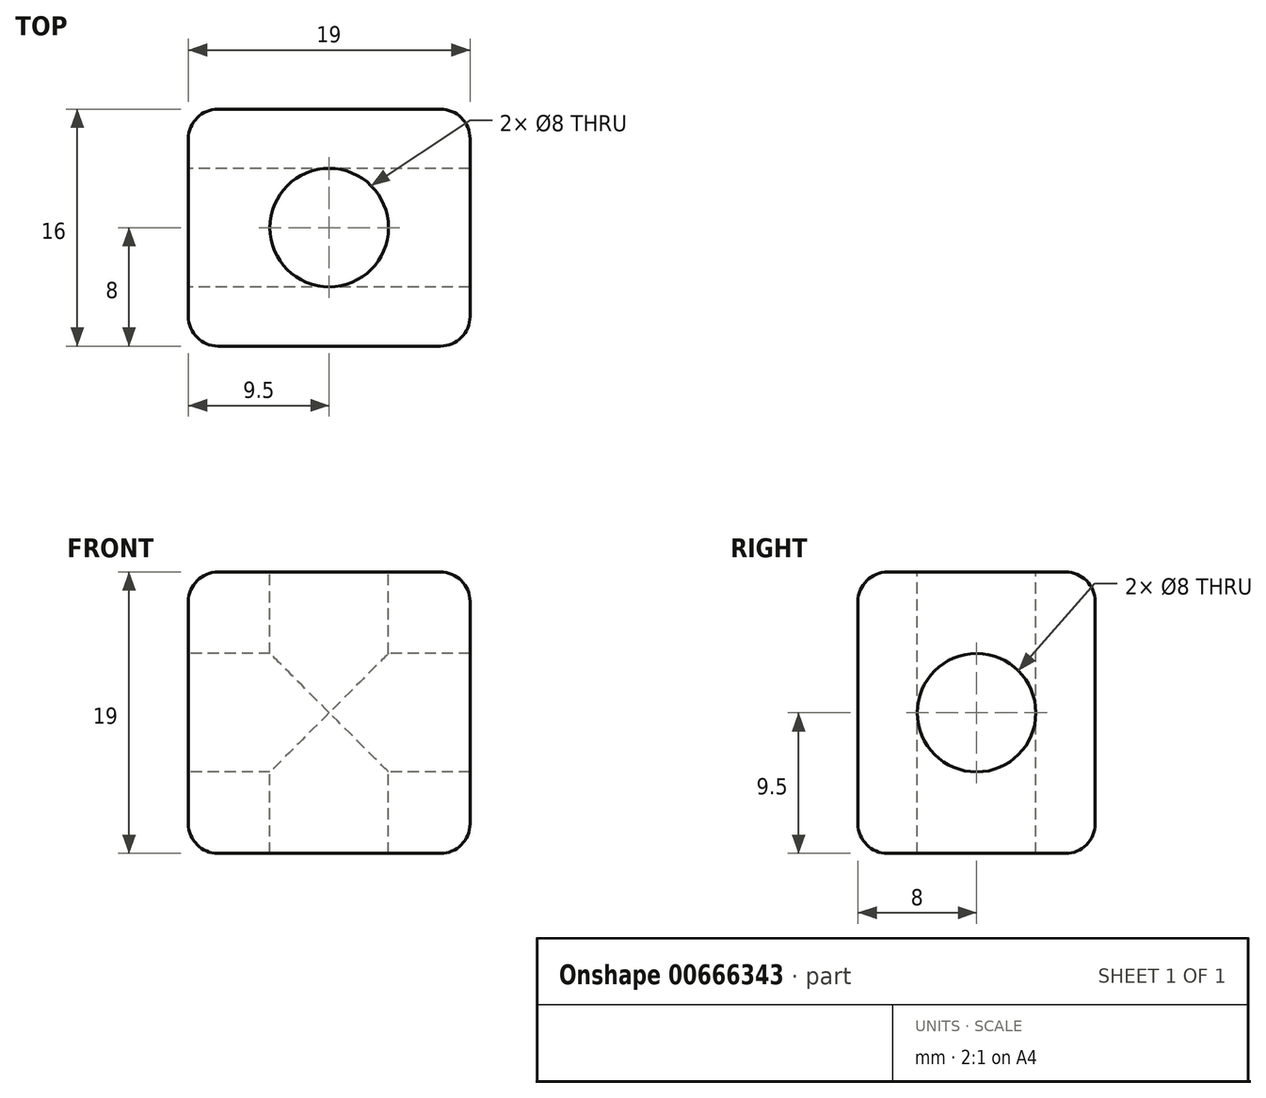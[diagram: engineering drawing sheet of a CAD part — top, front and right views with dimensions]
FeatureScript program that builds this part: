
annotation { "Feature Type Name" : "Feature", "Feature Type Description" : "" }
export const myFeature = defineFeature(function(context is Context, id is Id, definition is map)
    precondition{}
    {
        {
            var Q0;
            Q0=qCreatedBy(makeId("Front.planeOp"),FACE);
            var sketch = newSketch(context, id + "F0", { "sketchPlane" : qUnion([Q0])});
            skLineSegment(sketch, "E0.bottom", {"start": v(9.5, -9.5) * mm, "end": v(-9.5, -9.5) * mm});
            skLineSegment(sketch, "E0.top", {"start": v(9.5, 9.5) * mm, "end": v(-9.5, 9.5) * mm});
            skLineSegment(sketch, "E0.left", {"start": v(9.5, -9.5) * mm, "end": v(9.5, 9.5) * mm});
            skLineSegment(sketch, "E0.right", {"start": v(-9.5, -9.5) * mm, "end": v(-9.5, 9.5) * mm});
            skPoint(sketch, "E0.middle", {"position": v(0, 0) * mm});
            skSolve(sketch);
        }
        {
            var Q0;
            Q0=makeQuery(id+"F0.imprint","IMPRINT",FACE,{"disambiguationData":[TD([[makeQuery(id+"F0.imprint","IMPRINT",EDGE,{"derivedFrom":sQuery(id+"F0.wireOp",EDGE,"E0.bottom")}),-1.0]])]});
            extrude(context, id + "F1", {"entities" : qUnion([Q0]), "depth" : 16 * mm, "offsetDistance" : 25 * mm});
        }
        {
            var Q0;
            Q0=makeQuery(id+"F1.opExtrude","SWEPT_FACE",FACE,{"disambiguationData":[OSD([sQuery(id+"F0.wireOp",EDGE,"E0.top")])]});
            var sketch = newSketch(context, id + "F2", { "sketchPlane" : qUnion([Q0])});
            skCircle(sketch, "E1", {"center": v(0, -8) * mm, "radius": 4 * mm});
            skSolve(sketch);
        }
        {
            var Q0;
            Q0=makeQuery(id+"F2.imprint","IMPRINT",FACE,{"disambiguationData":[TD([[makeQuery(id+"F2.imprint","IMPRINT",EDGE,{"derivedFrom":sQuery(id+"F2.wireOp",EDGE,"E1")}),1.0]])]});
            extrude(context, id + "F3", {"entities" : qUnion([Q0]), "operationType" : NewBodyOperationType.REMOVE, "oppositeDirection" : true, "depth" : 19 * mm, "offsetDistance" : 25 * mm});
        }
        {
            var Q0;
            Q0=makeQuery(id+"F1.opExtrude","SWEPT_FACE",FACE,{"disambiguationData":[OSD([sQuery(id+"F0.wireOp",EDGE,"E0.right")])]});
            var sketch = newSketch(context, id + "F4", { "sketchPlane" : qUnion([Q0])});
            skCircle(sketch, "E2", {"center": v(8, 0) * mm, "radius": 4 * mm});
            skSolve(sketch);
        }
        {
            var Q0;
            Q0=makeQuery(id+"F4.imprint","IMPRINT",FACE,{"disambiguationData":[TD([[makeQuery(id+"F4.imprint","IMPRINT",EDGE,{"derivedFrom":sQuery(id+"F4.wireOp",EDGE,"E2")}),1.0]])]});
            extrude(context, id + "F5", {"entities" : qUnion([Q0]), "operationType" : NewBodyOperationType.REMOVE, "oppositeDirection" : true, "depth" : 19 * mm, "offsetDistance" : 25 * mm});
        }
        {
            var Q0;
            Q0=makeQuery(id+"F1.opExtrude","CAP_EDGE",EDGE,{"disambiguationData":[OSD([sQuery(id+"F0.wireOp",EDGE,"E0.left")])],"isStart":true});
            var Q1;
            Q1=makeQuery(id+"F1.opExtrude","CAP_EDGE",EDGE,{"disambiguationData":[OSD([sQuery(id+"F0.wireOp",EDGE,"E0.top")])],"isStart":true});
            var Q2;
            Q2=makeQuery(id+"F1.opExtrude","CAP_FACE",FACE,{"disambiguationData":[OSD([sQuery(id+"F0.wireOp",EDGE,"E0.bottom"),sQuery(id+"F0.wireOp",EDGE,"E0.top"),sQuery(id+"F0.wireOp",EDGE,"E0.left"),sQuery(id+"F0.wireOp",EDGE,"E0.right")])],"isStart":true});
            var Q3;
            Q3=makeQuery(id+"F1.opExtrude","CAP_EDGE",EDGE,{"disambiguationData":[OSD([sQuery(id+"F0.wireOp",EDGE,"E0.right")])],"isStart":false});
            var Q4;
            Q4=makeQuery(id+"F1.opExtrude","CAP_EDGE",EDGE,{"disambiguationData":[OSD([sQuery(id+"F0.wireOp",EDGE,"E0.left")])],"isStart":false});
            var Q5;
            Q5=makeQuery(id+"F1.opExtrude","CAP_EDGE",EDGE,{"disambiguationData":[OSD([sQuery(id+"F0.wireOp",EDGE,"E0.bottom")])],"isStart":false});
            var Q6;
            Q6=makeQuery(id+"F1.opExtrude","CAP_EDGE",EDGE,{"disambiguationData":[OSD([sQuery(id+"F0.wireOp",EDGE,"E0.top")])],"isStart":false});
            var Q7;
            Q7=makeQuery(id+"F1.opExtrude","SWEPT_EDGE",EDGE,{"disambiguationData":[OSD([sQuery(id+"F0.wireOp",EDGE,"E0.bottom"),sQuery(id+"F0.wireOp",EDGE,"E0.right")])]});
            var Q8;
            Q8=makeQuery(id+"F1.opExtrude","SWEPT_EDGE",EDGE,{"disambiguationData":[OSD([sQuery(id+"F0.wireOp",EDGE,"E0.bottom"),sQuery(id+"F0.wireOp",EDGE,"E0.left")])]});
            var Q9;
            Q9=makeQuery(id+"F1.opExtrude","SWEPT_EDGE",EDGE,{"disambiguationData":[OSD([sQuery(id+"F0.wireOp",EDGE,"E0.top"),sQuery(id+"F0.wireOp",EDGE,"E0.left")])]});
            var Q10;
            Q10=makeQuery(id+"F1.opExtrude","SWEPT_EDGE",EDGE,{"disambiguationData":[OSD([sQuery(id+"F0.wireOp",EDGE,"E0.top"),sQuery(id+"F0.wireOp",EDGE,"E0.right")])]});
            fillet(context, id + "F6", {"entities" : qUnion([Q0, Q1, Q2, Q3, Q4, Q5, Q6, Q7, Q8, Q9, Q10]), "radius" : 2 * mm, "tangentPropagation" : true, "allowEdgeOverflow" : false});
        }
    });
